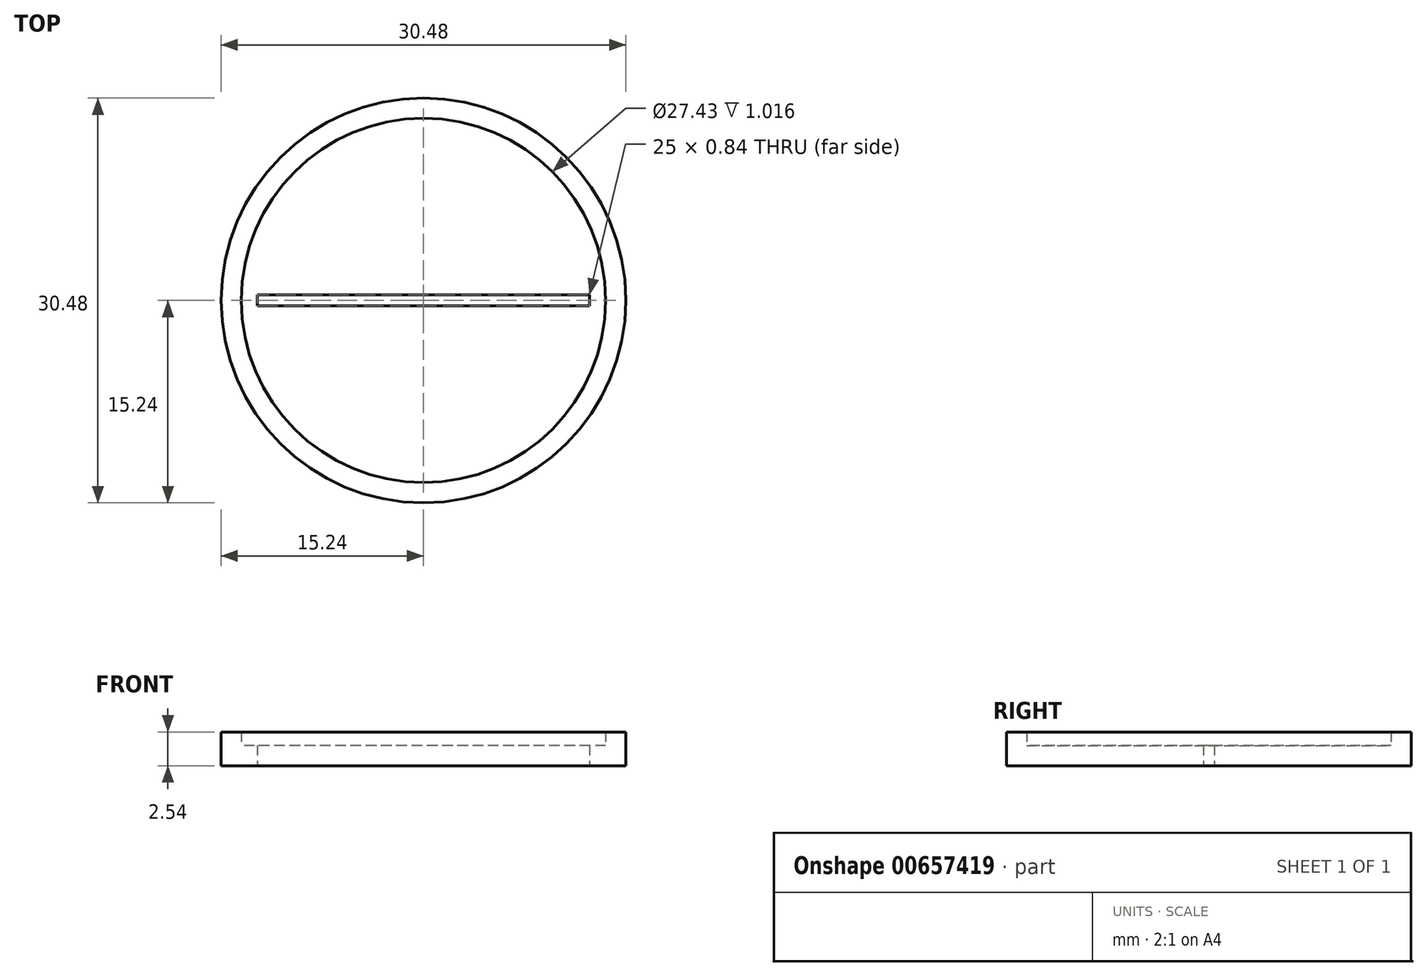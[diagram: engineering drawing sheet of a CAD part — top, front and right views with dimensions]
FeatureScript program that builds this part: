
annotation { "Feature Type Name" : "Feature", "Feature Type Description" : "" }
export const myFeature = defineFeature(function(context is Context, id is Id, definition is map)
    precondition{}
    {
        {
            var Q0;
            Q0=qCreatedBy(makeId("Top.planeOp"),FACE);
            var sketch = newSketch(context, id + "F0", { "sketchPlane" : qUnion([Q0])});
            skCircle(sketch, "E0", {"center": v(0, 0) * mm, "radius": 15.24 * mm});
            skLineSegment(sketch, "E1.bottom", {"start": v(12.5, 0.42) * mm, "end": v(-12.5, 0.42) * mm});
            skLineSegment(sketch, "E1.top", {"start": v(12.5, -0.42) * mm, "end": v(-12.5, -0.42) * mm});
            skLineSegment(sketch, "E1.left", {"start": v(12.5, 0.42) * mm, "end": v(12.5, -0.42) * mm});
            skLineSegment(sketch, "E1.right", {"start": v(-12.5, 0.42) * mm, "end": v(-12.5, -0.42) * mm});
            skCircle(sketch, "E2", {"center": v(0, 0) * mm, "radius": 13.72 * mm});
            skSolve(sketch);
        }
        {
            var Q0;
            Q0=makeQuery(id+"F0.imprint","IMPRINT",FACE,{"disambiguationData":[TD([[makeQuery(id+"F0.imprint","IMPRINT",EDGE,{"derivedFrom":sQuery(id+"F0.wireOp",EDGE,"E0")}),1.0]])]});
            extrude(context, id + "F1", {"entities" : qUnion([Q0]), "depth" : 2.54 * mm, "offsetDistance" : 25.4 * mm});
        }
        {
            var Q0;
            Q0=makeQuery(id+"F0.imprint","IMPRINT",FACE,{"disambiguationData":[TD([[makeQuery(id+"F0.imprint","IMPRINT",EDGE,{"derivedFrom":sQuery(id+"F0.wireOp",EDGE,"E1.bottom")}),-1.0]])]});
            extrude(context, id + "F2", {"entities" : qUnion([Q0]), "operationType" : NewBodyOperationType.ADD, "depth" : 1.52 * mm, "offsetDistance" : 25.4 * mm});
        }
        {
            var Q0;
            Q0=qCreatedBy(makeId("Top.planeOp"),FACE);
            cPlane(context, id + "F3", {"entities" : qUnion([Q0]), "cplaneType" : CPlaneType.OFFSET, "offset" : 25.4 * mm, "width" : 152.4 * mm, "height" : 152.4 * mm});
        }
    });
